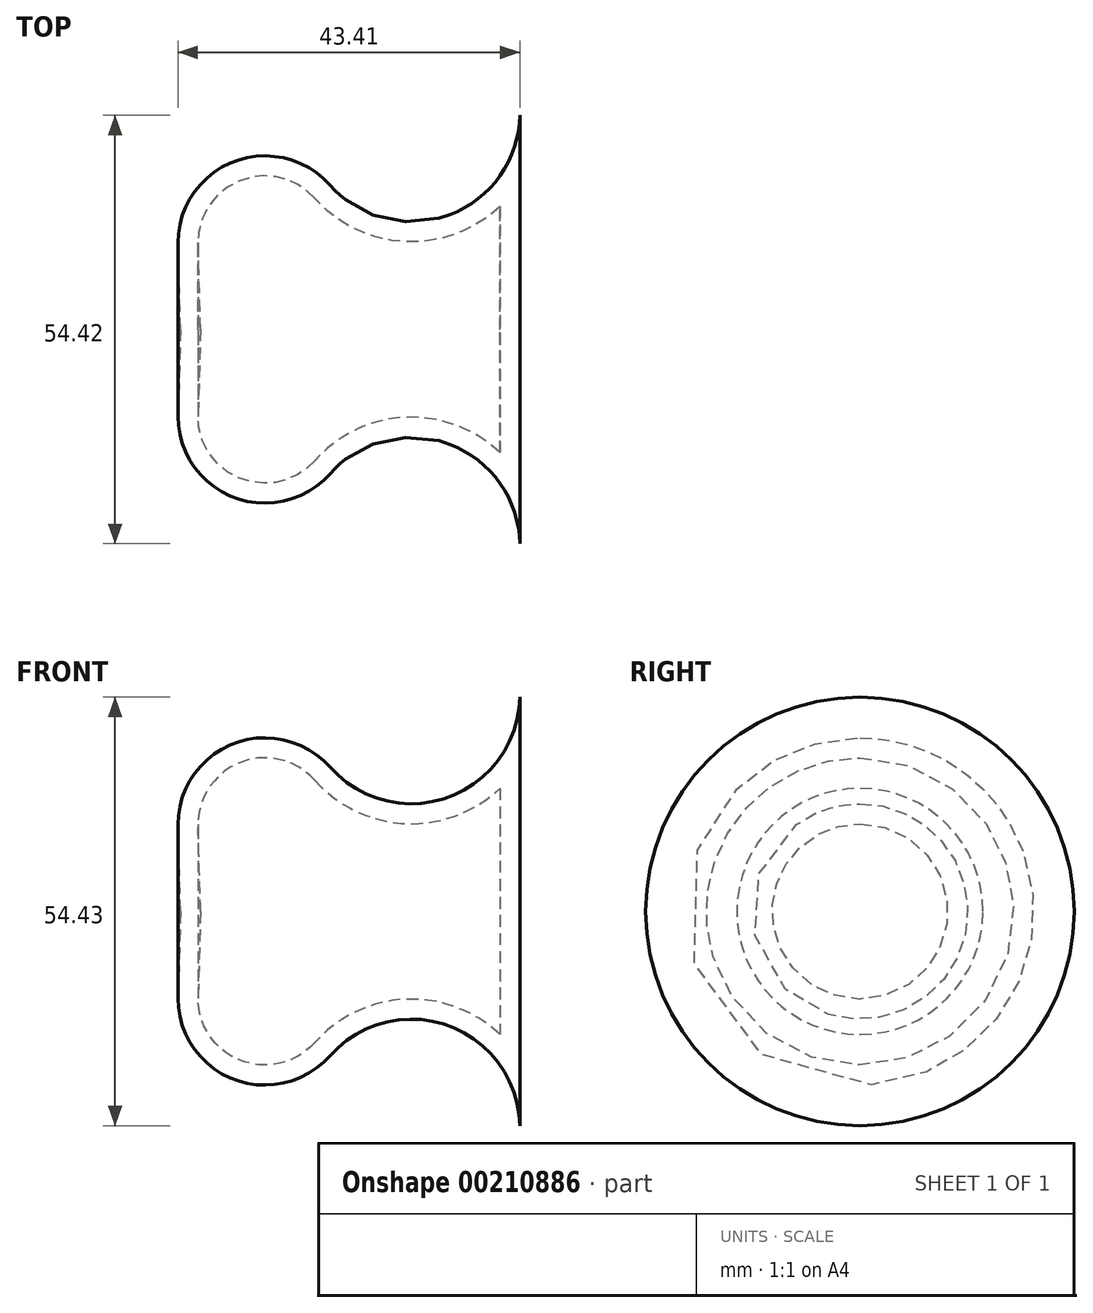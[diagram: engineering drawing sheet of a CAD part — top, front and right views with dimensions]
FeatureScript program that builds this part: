
annotation { "Feature Type Name" : "Feature", "Feature Type Description" : "" }
export const myFeature = defineFeature(function(context is Context, id is Id, definition is map)
    precondition{}
    {
        {
            var Q0;
            Q0=qCreatedBy(makeId("Front.planeOp"),FACE);
            var sketch = newSketch(context, id + "F0", { "sketchPlane" : qUnion([Q0])});
            skArc(sketch, "E0", {"start": v(-10.33, -9.14) * mm, "mid": v(4.76, -12.94) * mm, "end": v(13.8, -0.26) * mm});
            skArc(sketch, "E1", {"start": v(-10.33, -9.14) * mm, "mid": v(-22.65, -6.19) * mm, "end": v(-29.62, -16.77) * mm});
            skLineSegment(sketch, "E2", {"start": v(13.8, -0.26) * mm, "end": v(13.8, -27.48) * mm});
            skLineSegment(sketch, "E3", {"start": v(-29.3, -27.48) * mm, "end": v(-29.63, -16.45) * mm});
            skPoint(sketch, "E4.orphan", {"position": v(15.48, -27.48) * mm});
            skPoint(sketch, "E5.start.orphan", {"position": v(15.48, 0) * mm});
            skPoint(sketch, "E6.start.orphan", {"position": v(-18.6, -27.48) * mm});
            skLineSegment(sketch, "E7", {"start": v(-29.3, -27.48) * mm, "end": v(13.8, -27.48) * mm});
            skSolve(sketch);
        }
        {
            var Q0;
            Q0=makeQuery(id+"F0.imprint","IMPRINT",FACE,{"disambiguationData":[TD([[makeQuery(id+"F0.imprint","IMPRINT",EDGE,{"derivedFrom":sQuery(id+"F0.wireOp",EDGE,"E0")}),-1.0]])]});
            var Q1;
            Q1=sQuery(id+"F0.wireOp",EDGE,"E7");
            revolve(context, id + "F1", {"entities" : qUnion([Q0]), "axis" : qUnion([Q1]), "revolveType" : RevolveType.FULL});
        }
        {
            var Q0;
            Q0=makeQuery(id+"F1.opRevolve","SWEPT_FACE",FACE,{"disambiguationData":[OSD([sQuery(id+"F0.wireOp",EDGE,"E0")])]});
            var Q1;
            Q1=makeQuery(id+"F1.opRevolve","SWEPT_BODY",BODY,{"disambiguationData":[OSD([sQuery(id+"F0.wireOp",EDGE,"E0"),sQuery(id+"F0.wireOp",EDGE,"E1"),sQuery(id+"F0.wireOp",EDGE,"E2"),sQuery(id+"F0.wireOp",EDGE,"E3"),sQuery(id+"F0.wireOp",EDGE,"E7")])]});
            shell(context, id + "F2", {"isHollow" : true, "entities" : qUnion([Q0]), "parts" : qUnion([Q1]), "thickness" : 2.54 * mm});
        }
    });
